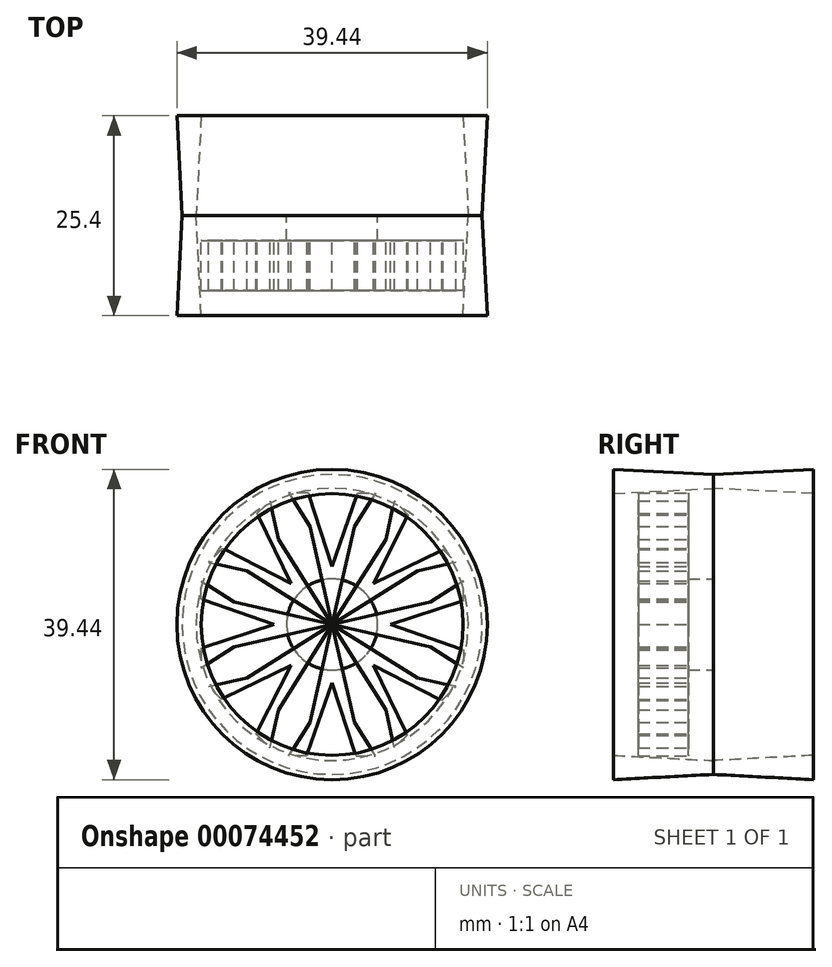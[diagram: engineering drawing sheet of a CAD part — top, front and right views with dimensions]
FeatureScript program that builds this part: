
annotation { "Feature Type Name" : "Feature", "Feature Type Description" : "" }
export const myFeature = defineFeature(function(context is Context, id is Id, definition is map)
    precondition{}
    {
        {
            var Q0;
            Q0=qCreatedBy(makeId("Front.planeOp"),FACE);
            var sketch = newSketch(context, id + "F0", { "sketchPlane" : qUnion([Q0])});
            skCircle(sketch, "E0", {"center": v(0, 0) * mm, "radius": 19.05 * mm});
            skCircle(sketch, "E1", {"center": v(0, 0) * mm, "radius": 17.29 * mm});
            skSolve(sketch);
        }
        {
            var Q0;
            Q0 = qSketchRegion(id + "F0", true);
            extrude(context, id + "F1", {"entities" : qUnion([Q0]), "endBound" : BoundingType.SYMMETRIC, "depth" : 25.4 * mm, "hasDraft" : true, "draftAngle" : 3 * degree});
        }
        {
            var Q0;
            Q0=qCreatedBy(makeId("Front.planeOp"),FACE);
            var sketch = newSketch(context, id + "F2", { "sketchPlane" : qUnion([Q0])});
            skCircle(sketch, "E2", {"center": v(0, 0) * mm, "radius": 5.78 * mm});
            skSolve(sketch);
        }
        {
            var Q0;
            Q0 = qSketchRegion(id + "F2", true);
            extrude(context, id + "F3", {"entities" : qUnion([Q0]), "depth" : 3.17 * mm});
        }
        {
            var Q0;
            Q0=qCreatedBy(makeId("Front.planeOp"),FACE);
            cPlane(context, id + "F4", {"entities" : qUnion([Q0]), "cplaneType" : CPlaneType.OFFSET, "offset" : 3.17 * mm, "width" : 152.4 * mm, "height" : 152.4 * mm});
        }
        {
            var Q0;
            Q0=qCreatedBy(id+"F4.planeOp",FACE);
            var sketch = newSketch(context, id + "F5", { "sketchPlane" : qUnion([Q0])});
            skLineSegment(sketch, "E3", {"start": v(0, 0) * mm, "end": v(7.4, 0) * mm});
            skLineSegment(sketch, "E4", {"start": v(16.68, 3.01) * mm, "end": v(16.68, 5.52) * mm});
            skLineSegment(sketch, "E5", {"start": v(16.68, 5.52) * mm, "end": v(12.47, 2.84) * mm});
            skLineSegment(sketch, "E6", {"start": v(12.47, 2.84) * mm, "end": v(0, 0) * mm});
            skLineSegment(sketch, "E7.MirrorCS", {"start": v(16.68, -5.52) * mm, "end": v(12.47, -2.84) * mm});
            skLineSegment(sketch, "E8.MirrorCS", {"start": v(16.68, -3.22) * mm, "end": v(16.68, -5.52) * mm});
            skLineSegment(sketch, "E9.MirrorCS", {"start": v(12.47, -2.84) * mm, "end": v(0, 0) * mm});
            skLineSegment(sketch, "E10", {"start": v(16.68, 3.01) * mm, "end": v(7.4, 0) * mm});
            skLineSegment(sketch, "E11", {"start": v(7.4, 0) * mm, "end": v(16.68, -3.22) * mm});
            skPoint(sketch, "E12.orphan", {"position": v(16.68, 0) * mm});
            skSolve(sketch);
        }
        {
            var Q0;
            Q0 = qSketchRegion(id + "F5", true);
            extrude(context, id + "F6", {"entities" : qUnion([Q0]), "depth" : 6.35 * mm});
        }
        {
            var Q0;
            Q0=makeQuery(id+"F6.opExtrude","SWEPT_BODY",BODY,{"disambiguationData":[OSD([sQuery(id+"F5.wireOp",EDGE,"E4"),sQuery(id+"F5.wireOp",EDGE,"E5"),sQuery(id+"F5.wireOp",EDGE,"E6"),sQuery(id+"F5.wireOp",EDGE,"E7.MirrorCS"),sQuery(id+"F5.wireOp",EDGE,"E8.MirrorCS"),sQuery(id+"F5.wireOp",EDGE,"E9.MirrorCS"),sQuery(id+"F5.wireOp",EDGE,"E10"),sQuery(id+"F5.wireOp",EDGE,"E11")])]});
            var Q1;
            Q1=makeQuery(id+"F3.opExtrude","CAP_EDGE",EDGE,{"disambiguationData":[OSD([sQuery(id+"F2.wireOp",EDGE,"E2")])],"isStart":false});
            circularPattern(context, id + "F7", {"entities" : qUnion([Q0]), "axis" : qUnion([Q1]), "angle" : 45 * degree, "instanceCount" : 8});
        }
    });
